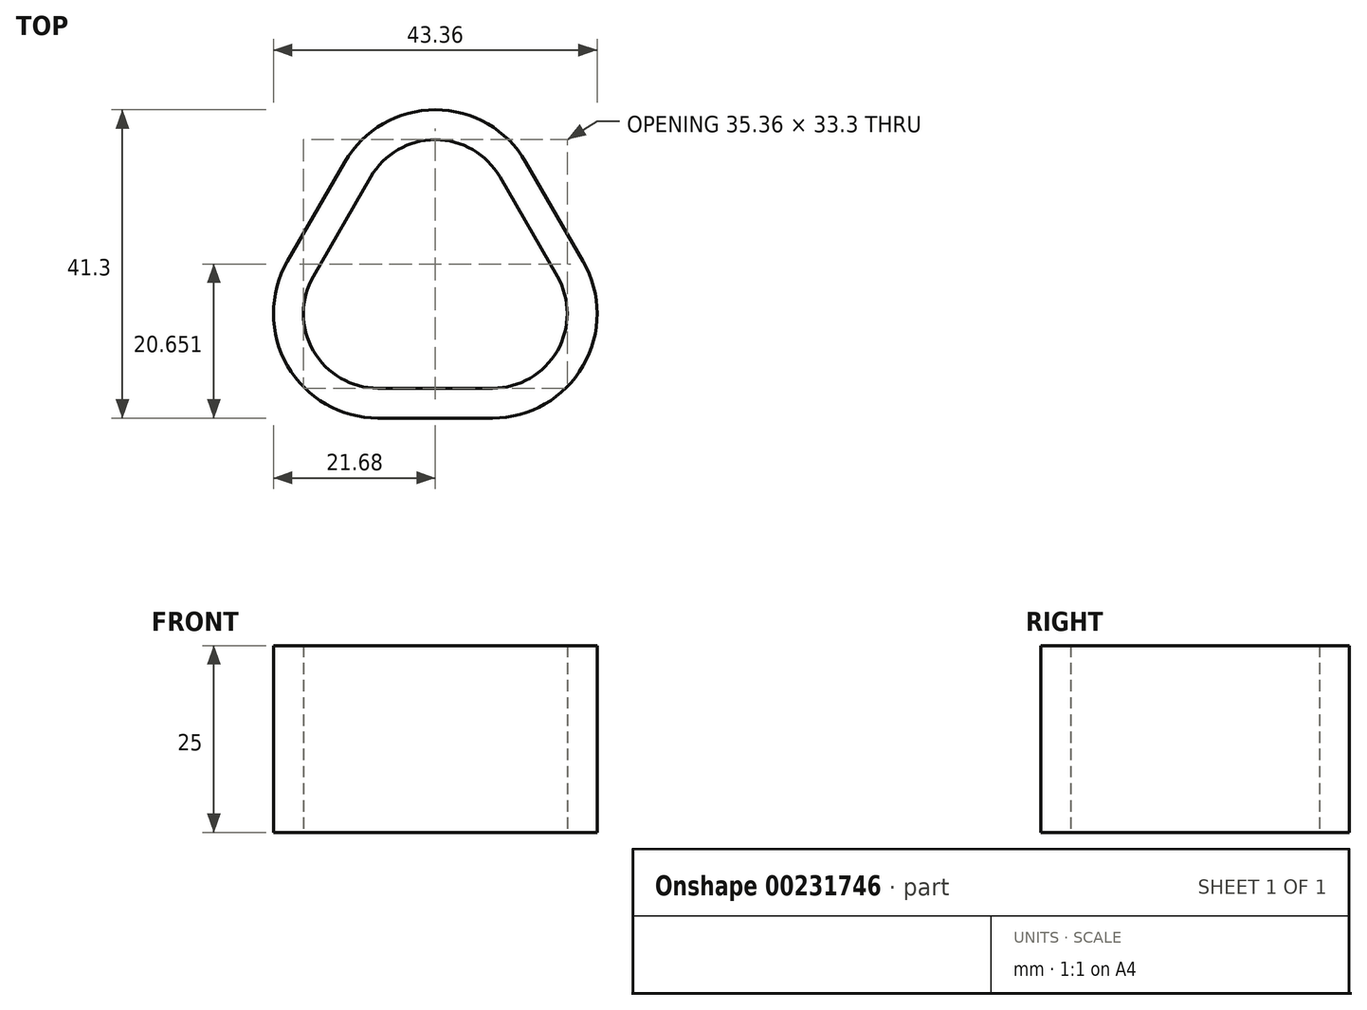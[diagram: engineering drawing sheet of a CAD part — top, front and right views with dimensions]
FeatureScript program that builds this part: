
annotation { "Feature Type Name" : "Feature", "Feature Type Description" : "" }
export const myFeature = defineFeature(function(context is Context, id is Id, definition is map)
    precondition{}
    {
        {
            var Q0;
            Q0=qCreatedBy(makeId("Top.planeOp"),FACE);
            var sketch = newSketch(context, id + "F0", { "sketchPlane" : qUnion([Q0])});
            skLineSegment(sketch, "E0", {"start": v(0, 0) * mm, "end": v(7.68, 0) * mm});
            skLineSegment(sketch, "E1", {"start": v(16.34, 15) * mm, "end": v(8.66, 28.3) * mm});
            skLineSegment(sketch, "E2", {"start": v(-8.66, 28.3) * mm, "end": v(-16.34, 15) * mm});
            skLineSegment(sketch, "E3", {"start": v(-7.68, 0) * mm, "end": v(0, 0) * mm});
            skLineSegment(sketch, "E4", {"start": v(0, 0) * mm, "end": v(0, 43.3) * mm, "construction": true});
            skLineSegment(sketch, "E5", {"start": v(-12.5, 21.65) * mm, "end": v(25, 0) * mm, "construction": true});
            skLineSegment(sketch, "E6", {"start": v(12.5, 21.65) * mm, "end": v(-25, 0) * mm, "construction": true});
            skCircle(sketch, "E7", {"center": v(0, 14.43) * mm, "radius": 12.5 * mm});
            skPoint(sketch, "E8.visualSharp", {"position": v(0, 43.3) * mm});
            skArc(sketch, "E8.filletArc", {"start": v(8.66, 28.3) * mm, "mid": v(0, 33.3) * mm, "end": v(-8.66, 28.3) * mm});
            skPoint(sketch, "E9.visualSharp", {"position": v(-25, 0) * mm});
            skArc(sketch, "E9.filletArc", {"start": v(-16.34, 15) * mm, "mid": v(-16.34, 5) * mm, "end": v(-7.68, 0) * mm});
            skPoint(sketch, "E10.visualSharp", {"position": v(25, 0) * mm});
            skArc(sketch, "E10.filletArc", {"start": v(7.68, 0) * mm, "mid": v(16.34, 5) * mm, "end": v(16.34, 15) * mm});
            skLineSegment(sketch, "E11.0", {"start": v(19.8, 17) * mm, "end": v(12.12, 30.3) * mm});
            skArc(sketch, "E11.1", {"start": v(7.68, -4) * mm, "mid": v(19.8, 3) * mm, "end": v(19.8, 17) * mm});
            skLineSegment(sketch, "E11.2", {"start": v(-12.12, 30.3) * mm, "end": v(-19.8, 17) * mm});
            skArc(sketch, "E11.3", {"start": v(-19.8, 17) * mm, "mid": v(-19.8, 3) * mm, "end": v(-7.68, -4) * mm});
            skLineSegment(sketch, "E11.4", {"start": v(-7.68, -4) * mm, "end": v(0, -4) * mm});
            skArc(sketch, "E11.5", {"start": v(12.12, 30.3) * mm, "mid": v(0, 37.3) * mm, "end": v(-12.12, 30.3) * mm});
            skLineSegment(sketch, "E11.6", {"start": v(0, -4) * mm, "end": v(7.68, -4) * mm});
            skSolve(sketch);
        }
        {
            var Q0;
            Q0=makeQuery(id+"F0.imprint","IMPRINT",FACE,{"disambiguationData":[TD([[makeQuery(id+"F0.imprint","IMPRINT",EDGE,{"derivedFrom":sQuery(id+"F0.wireOp",EDGE,"E0")}),-1.0]])]});
            extrude(context, id + "F1", {"entities" : qUnion([Q0]), "depth" : 25 * mm});
        }
    });
